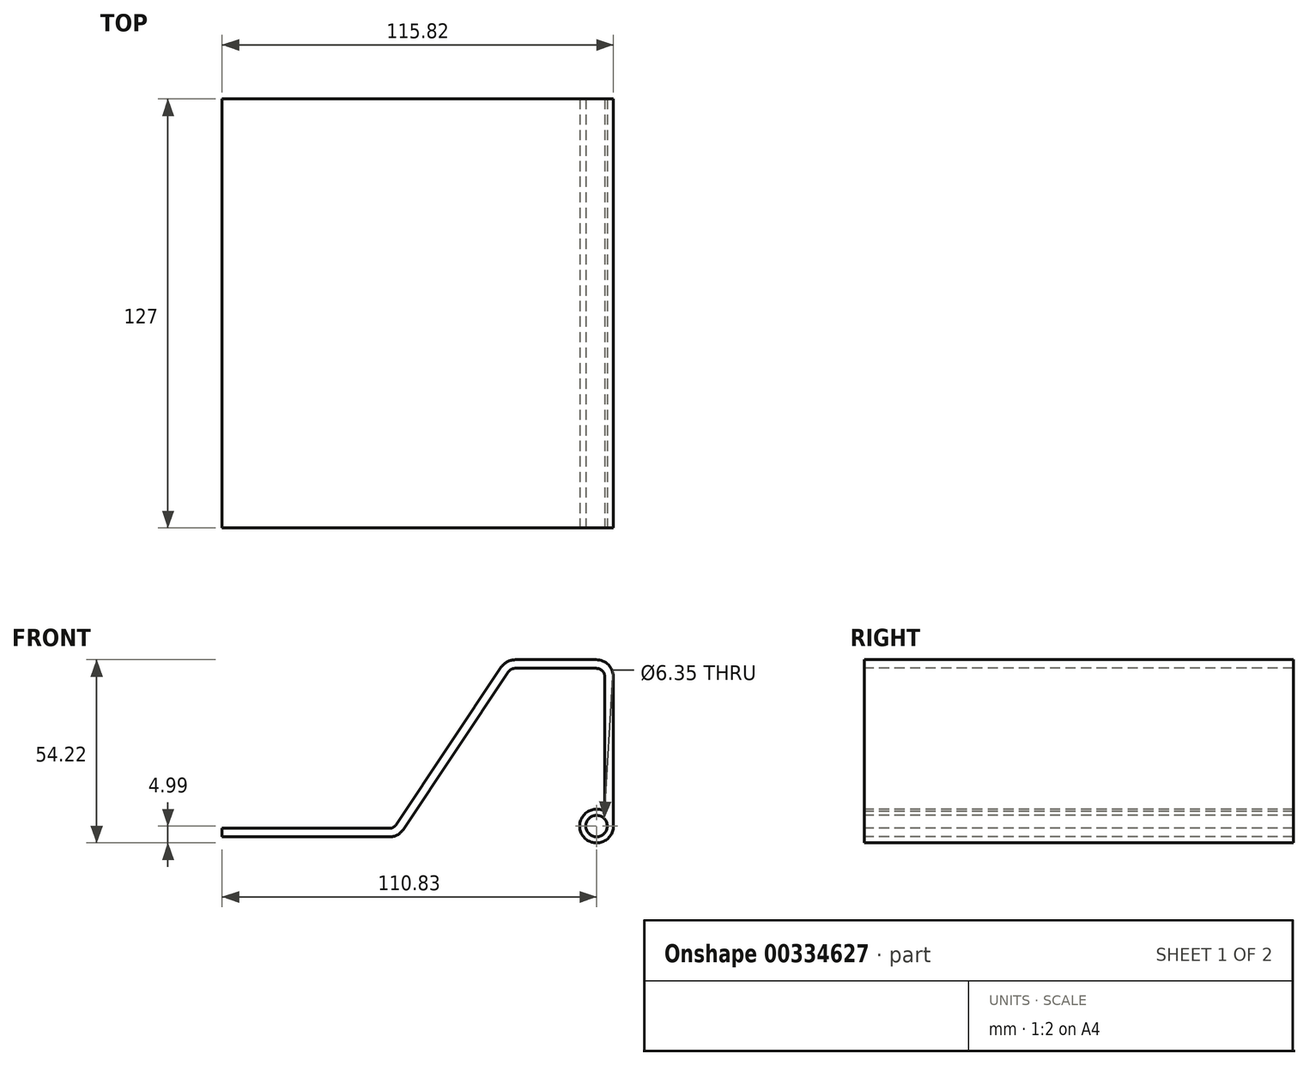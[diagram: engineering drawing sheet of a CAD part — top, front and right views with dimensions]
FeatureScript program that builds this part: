
annotation { "Feature Type Name" : "Feature", "Feature Type Description" : "" }
export const myFeature = defineFeature(function(context is Context, id is Id, definition is map)
    precondition{}
    {
        {
            var Q0;
            Q0=qCreatedBy(makeId("Front.planeOp"),FACE);
            var sketch = newSketch(context, id + "F0", { "sketchPlane" : qUnion([Q0])});
            skCircle(sketch, "E0", {"center": v(0, 0) * mm, "radius": 5 * mm});
            skCircle(sketch, "E1", {"center": v(0, 0) * mm, "radius": 3.18 * mm});
            skLineSegment(sketch, "E2", {"start": v(5, 0) * mm, "end": v(5, 49.23) * mm});
            skLineSegment(sketch, "E3", {"start": v(5, 49.23) * mm, "end": v(-26.76, 49.23) * mm});
            skLineSegment(sketch, "E4", {"start": v(-26.76, 49.23) * mm, "end": v(-60.03, -0.69) * mm});
            skLineSegment(sketch, "E5", {"start": v(-60.03, -0.69) * mm, "end": v(-110.83, -0.69) * mm});
            skLineSegment(sketch, "E6", {"start": v(-110.83, -0.69) * mm, "end": v(-110.83, -3.23) * mm});
            skLineSegment(sketch, "E7", {"start": v(-110.83, -3.23) * mm, "end": v(-58.67, -3.23) * mm});
            skLineSegment(sketch, "E8", {"start": v(-58.67, -3.23) * mm, "end": v(-25.4, 46.69) * mm});
            skLineSegment(sketch, "E9", {"start": v(-25.4, 46.69) * mm, "end": v(2.45, 46.69) * mm});
            skLineSegment(sketch, "E10", {"start": v(2.45, 46.69) * mm, "end": v(2.45, 4.35) * mm});
            skSolve(sketch);
        }
        {
            var Q0;
            {var subQ0=sQuery(id+"F0.wireOp",EDGE,"E2");Q0=makeQuery(id+"F0.imprint","IMPRINT",FACE,{"disambiguationData":[TD([[makeQuery(id+"F0.imprint","IMPRINT",EDGE,{"derivedFrom":subQ0}),1.0]])]});}
            var Q1;
            Q1=makeQuery(id+"F0.imprint","IMPRINT",FACE,{"disambiguationData":[TD([[makeQuery(id+"F0.imprint","IMPRINT",EDGE,{"derivedFrom":sQuery(id+"F0.wireOp",EDGE,"E1")}),-1.0]])]});
            extrude(context, id + "F1", {"entities" : qUnion([Q0, Q1]), "oppositeDirection" : true, "depth" : 127 * mm});
        }
        {
            var Q0;
            Q0=makeQuery(id+"F1.opExtrude","SWEPT_EDGE",EDGE,{"disambiguationData":[OSD([sQuery(id+"F0.wireOp",EDGE,"E3"),sQuery(id+"F0.wireOp",EDGE,"E4")])]});
            var Q1;
            Q1=makeQuery(id+"F1.opExtrude","SWEPT_EDGE",EDGE,{"disambiguationData":[OSD([sQuery(id+"F0.wireOp",EDGE,"E2"),sQuery(id+"F0.wireOp",EDGE,"E3")])]});
            var Q2;
            Q2=makeQuery(id+"F1.opExtrude","SWEPT_EDGE",EDGE,{"disambiguationData":[OSD([sQuery(id+"F0.wireOp",EDGE,"E7"),sQuery(id+"F0.wireOp",EDGE,"E8")])]});
            fillet(context, id + "F2", {"entities" : qUnion([Q0, Q1, Q2]), "radius" : 5.08 * mm, "tangentPropagation" : true, "allowEdgeOverflow" : false});
        }
        {
            var Q0;
            Q0=makeQuery(id+"F1.opExtrude","SWEPT_EDGE",EDGE,{"disambiguationData":[OSD([sQuery(id+"F0.wireOp",EDGE,"E9"),sQuery(id+"F0.wireOp",EDGE,"E10")])]});
            var Q1;
            Q1=makeQuery(id+"F1.opExtrude","SWEPT_EDGE",EDGE,{"disambiguationData":[OSD([sQuery(id+"F0.wireOp",EDGE,"E8"),sQuery(id+"F0.wireOp",EDGE,"E9")])]});
            var Q2;
            Q2=makeQuery(id+"F1.opExtrude","SWEPT_EDGE",EDGE,{"disambiguationData":[OSD([sQuery(id+"F0.wireOp",EDGE,"E4"),sQuery(id+"F0.wireOp",EDGE,"E5")])]});
            fillet(context, id + "F3", {"entities" : qUnion([Q0, Q1, Q2]), "radius" : 2.54 * mm, "tangentPropagation" : true, "allowEdgeOverflow" : false});
        }
    });
